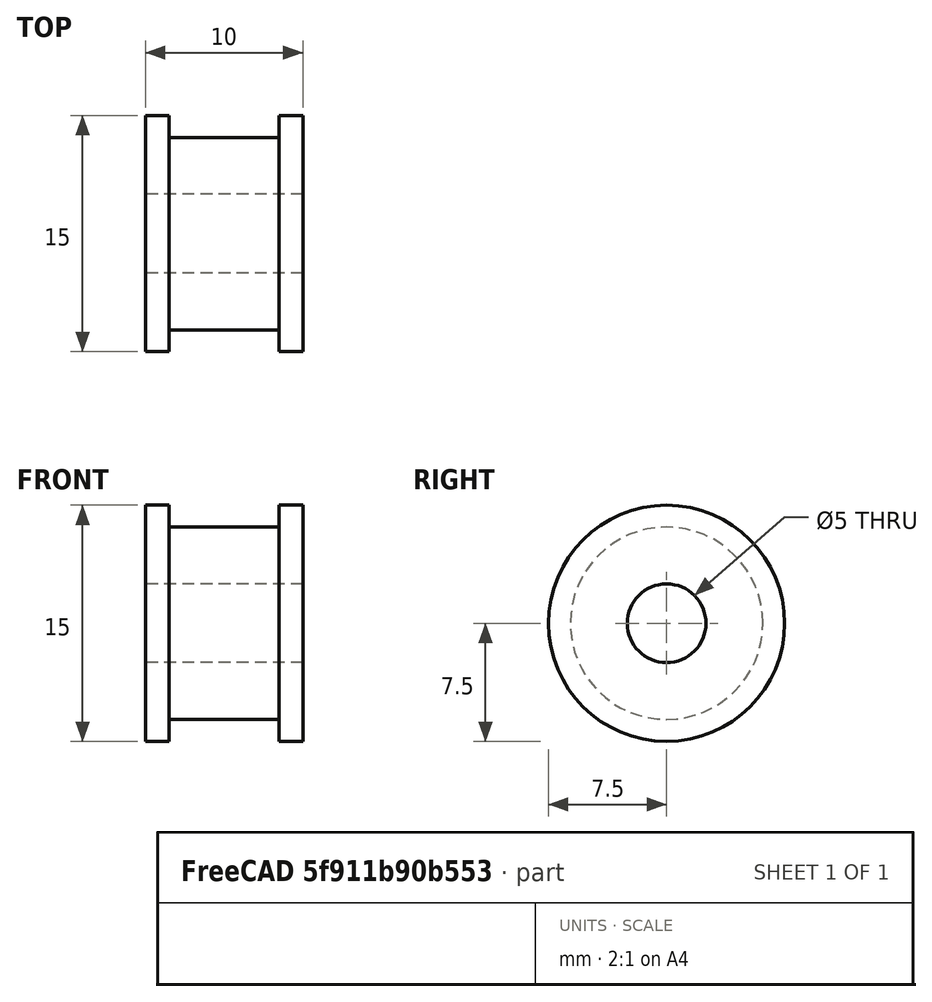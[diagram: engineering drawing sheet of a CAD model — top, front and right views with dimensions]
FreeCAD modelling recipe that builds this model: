
FCSTD DOCUMENT  (FreeCAD 0.19R23578 (Git))
Label: gates_2gt_idler_toothed
License: All rights reserved
LicenseURL: http://en.wikipedia.org/wiki/All_rights_reserved
objects: Sketcher::SketchObject×1, PartDesign::Revolution×1, PartDesign::Body×1, PartDesign::CoordinateSystem×1, App::Part×1
note: 5 computed .brp shape members not serialized (recipe doc carries the construction recipe); baked Part::Feature solids carry a one-line shape summary decoded from their .brp

FEATURE [Sketcher::SketchObject] Sketch069
  MapMode = 5
  Support = -> [XY_Plane079]
  sketch-geometry (8):
    g0: LineSegment StartX=-3.5 StartY=7.5 StartZ=0 EndX=-3.5 EndY=6.11 EndZ=0
    g1: LineSegment StartX=-3.5 StartY=6.11 StartZ=0 EndX=3.5 EndY=6.11 EndZ=0
    g2: LineSegment StartX=3.5 StartY=6.11 StartZ=0 EndX=3.5 EndY=7.5 EndZ=0
    g3: LineSegment StartX=3.5 StartY=7.5 StartZ=0 EndX=5 EndY=7.5 EndZ=0
    g4: LineSegment StartX=5 StartY=7.5 StartZ=0 EndX=5 EndY=2.5 EndZ=0
    g5: LineSegment StartX=5 StartY=2.5 StartZ=0 EndX=-5 EndY=2.5 EndZ=0
    g6: LineSegment StartX=-5 StartY=2.5 StartZ=0 EndX=-5 EndY=7.5 EndZ=0
    g7: LineSegment StartX=-5 StartY=7.5 StartZ=0 EndX=-3.5 EndY=7.5 EndZ=0
  constraints (20):
    c: Coincident(g0,g1)
    c: Coincident(g1,g2)
    c: Coincident(g2,g3)
    c: Horizontal(g3)
    c: Coincident(g3,g4)
    c: Coincident(g4,g5)
    c: Coincident(g5,g6)
    c: Coincident(g6,g7)
    c: Coincident(g0,g7)
    c: Vertical(g6)
    c: Vertical(g0)
    c: Symmetric(g0,g1,g-2)
    c: Symmetric(g0,g2,g-2)
    c: Symmetric(g6,g3,g-2)
    c: Symmetric(g5,g4,g-2)
    c: DistanceX(g1,g1) = 7
    c: DistanceX(g5,g5) = 10
    c: DistanceY(g-1,g4) = 2.5
    c: DistanceY(g-1,g1) = 6.11
    c: DistanceY(g-1,g3) = 7.5
FEATURE [PartDesign::Revolution] Revolution002
  AllowMultiFace = false
  Angle = 360
  Axis = (1,0,0)
  Base = (0,0,0)
  Profile = -> Sketch069
  ReferenceAxis = -> X_Axis079
FEATURE [PartDesign::Body] Body025  label="Body"
  Group = -> [Sketch069,Revolution002]
  Origin = -> Origin079
  Tip = -> Revolution002
FEATURE [PartDesign::CoordinateSystem] LCS_1
  AttacherType = Attacher::AttachEngine3D
  MapMode = 45
  Placement = pos=(0,1.19e-14,1e-16) rot=(-0.57735,-0.57735,-0.57735;2.0944rad)
  Support = -> [Revolution002]
FEATURE [App::Part] Part042  label="e3d_2gt_idler"
  Group = -> [Body025,LCS_1]
  Origin = -> Origin078
